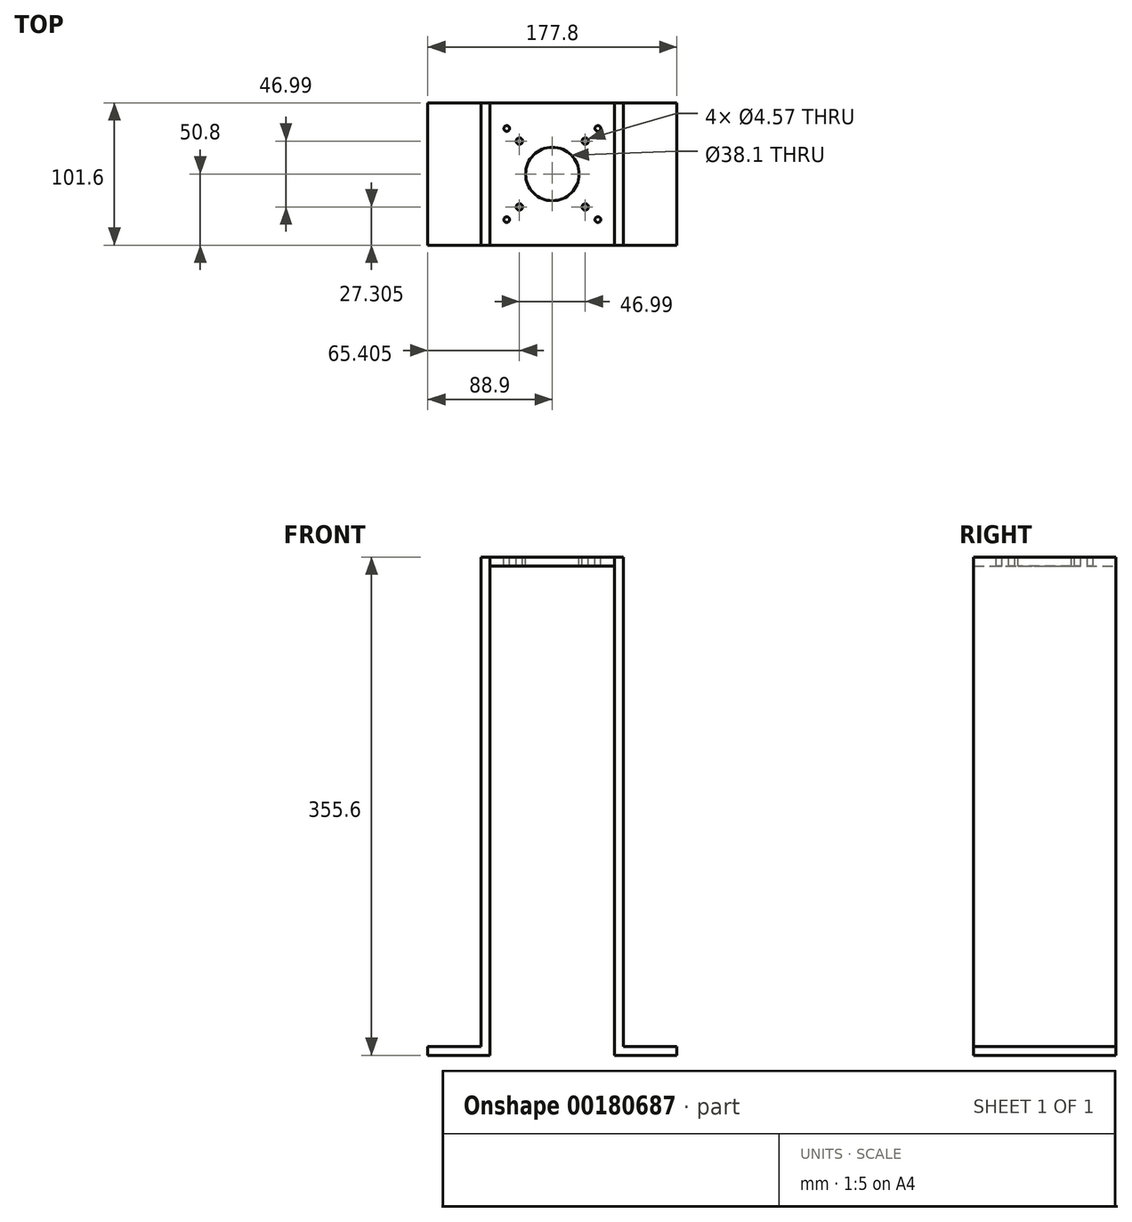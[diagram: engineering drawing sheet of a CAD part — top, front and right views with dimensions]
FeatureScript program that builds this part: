
annotation { "Feature Type Name" : "Feature", "Feature Type Description" : "" }
export const myFeature = defineFeature(function(context is Context, id is Id, definition is map)
    precondition{}
    {
        {
            var Q0;
            Q0=qCreatedBy(makeId("Top.planeOp"),FACE);
            cPlane(context, id + "F0", {"entities" : qUnion([Q0]), "cplaneType" : CPlaneType.OFFSET, "offset" : 152.4 * mm, "width" : 152.4 * mm, "height" : 152.4 * mm});
        }
        {
            var Q0;
            Q0=qCreatedBy(id+"F0.planeOp",FACE);
            var sketch = newSketch(context, id + "F1", { "sketchPlane" : qUnion([Q0])});
            skLineSegment(sketch, "E0.bottom", {"start": v(50.8, 50.8) * mm, "end": v(-50.8, 50.8) * mm});
            skLineSegment(sketch, "E0.top", {"start": v(50.8, -50.8) * mm, "end": v(-50.8, -50.8) * mm});
            skLineSegment(sketch, "E0.left", {"start": v(50.8, 50.8) * mm, "end": v(50.8, -50.8) * mm});
            skLineSegment(sketch, "E0.right", {"start": v(-50.8, 50.8) * mm, "end": v(-50.8, -50.8) * mm});
            skPoint(sketch, "E0.middle", {"position": v(0, 0) * mm});
            skLineSegment(sketch, "E1", {"start": v(-44.45, 50.8) * mm, "end": v(-44.45, -50.8) * mm});
            skLineSegment(sketch, "E2", {"start": v(44.45, -50.8) * mm, "end": v(44.45, 50.8) * mm});
            skCircle(sketch, "E3", {"center": v(0, 0) * mm, "radius": 19.05 * mm});
            skCircle(sketch, "E4", {"center": v(-23.5, 23.5) * mm, "radius": 2.29 * mm});
            skCircle(sketch, "E5.0.1.0", {"center": v(-23.5, -23.5) * mm, "radius": 2.29 * mm});
            skCircle(sketch, "E5.1.0.0", {"center": v(23.5, 23.5) * mm, "radius": 2.29 * mm});
            skCircle(sketch, "E5.1.1.0", {"center": v(23.5, -23.5) * mm, "radius": 2.29 * mm});
            skLineSegment(sketch, "E5.direction1", {"start": v(-23.5, 23.5) * mm, "end": v(23.5, 23.5) * mm, "construction": true});
            skLineSegment(sketch, "E5.direction2", {"start": v(-23.5, 23.5) * mm, "end": v(-23.5, -23.5) * mm, "construction": true});
            skCircle(sketch, "E6", {"center": v(-32.51, 32.51) * mm, "radius": 2.03 * mm});
            skCircle(sketch, "E7.0.1.0", {"center": v(-32.51, -32.51) * mm, "radius": 2.03 * mm});
            skCircle(sketch, "E7.1.0.0", {"center": v(32.51, 32.51) * mm, "radius": 2.03 * mm});
            skCircle(sketch, "E7.1.1.0", {"center": v(32.51, -32.51) * mm, "radius": 2.03 * mm});
            skLineSegment(sketch, "E7.direction1", {"start": v(-32.51, 32.51) * mm, "end": v(32.51, 32.51) * mm, "construction": true});
            skLineSegment(sketch, "E7.direction2", {"start": v(-32.51, 32.51) * mm, "end": v(-32.51, -32.51) * mm, "construction": true});
            skSolve(sketch);
        }
        {
            var Q0;
            {var subQ0=sQuery(id+"F1.wireOp",EDGE,"E1");Q0=makeQuery(id+"F1.imprint","IMPRINT",FACE,{"disambiguationData":[TD([[makeQuery(id+"F1.imprint","IMPRINT",EDGE,{"derivedFrom":subQ0}),1.0]])]});}
            extrude(context, id + "F2", {"entities" : qUnion([Q0]), "oppositeDirection" : true, "depth" : 6.35 * mm});
        }
        {
            var Q0;
            {var subQ0=sQuery(id+"F1.wireOp",EDGE,"E0.right");Q0=makeQuery(id+"F1.imprint","IMPRINT",FACE,{"disambiguationData":[TD([[makeQuery(id+"F1.imprint","IMPRINT",EDGE,{"derivedFrom":subQ0}),1.0]])]});}
            var Q1;
            {var subQ0=sQuery(id+"F1.wireOp",EDGE,"E0.left");Q1=makeQuery(id+"F1.imprint","IMPRINT",FACE,{"disambiguationData":[TD([[makeQuery(id+"F1.imprint","IMPRINT",EDGE,{"derivedFrom":subQ0}),-1.0]])]});}
            extrude(context, id + "F3", {"entities" : qUnion([Q0, Q1]), "oppositeDirection" : true, "depth" : 355.6 * mm});
        }
        {
            var Q0;
            Q0=makeQuery(id+"F3.opExtrude","SWEPT_FACE",FACE,{"disambiguationData":[OSD([sQuery(id+"F1.wireOp",EDGE,"E0.left")])]});
            var sketch = newSketch(context, id + "F4", { "sketchPlane" : qUnion([Q0])});
            skLineSegment(sketch, "E8", {"start": v(-50.8, -196.85) * mm, "end": v(50.8, -196.85) * mm});
            skSolve(sketch);
        }
        {
            var Q0;
            Q0=makeQuery(id+"F3.opExtrude","SWEPT_FACE",FACE,{"disambiguationData":[OSD([sQuery(id+"F1.wireOp",EDGE,"E0.right")])]});
            var sketch = newSketch(context, id + "F5", { "sketchPlane" : qUnion([Q0])});
            skLineSegment(sketch, "E9", {"start": v(-50.8, -196.85) * mm, "end": v(50.8, -196.85) * mm});
            skSolve(sketch);
        }
        {
            var Q0;
            {var subQ0=sQuery(id+"F4.wireOp",EDGE,"E8");Q0=makeQuery(id+"F4.imprint","IMPRINT",FACE,{"disambiguationData":[TD([[makeQuery(id+"F4.imprint","IMPRINT",EDGE,{"derivedFrom":subQ0}),-1.0]])]});}
            extrude(context, id + "F6", {"entities" : qUnion([Q0]), "operationType" : NewBodyOperationType.ADD, "depth" : 38.1 * mm});
        }
        {
            var Q0;
            {var subQ0=sQuery(id+"F5.wireOp",EDGE,"E9");Q0=makeQuery(id+"F5.imprint","IMPRINT",FACE,{"disambiguationData":[TD([[makeQuery(id+"F5.imprint","IMPRINT",EDGE,{"derivedFrom":subQ0}),-1.0]])]});}
            extrude(context, id + "F7", {"entities" : qUnion([Q0]), "operationType" : NewBodyOperationType.ADD, "depth" : 38.1 * mm});
        }
    });
